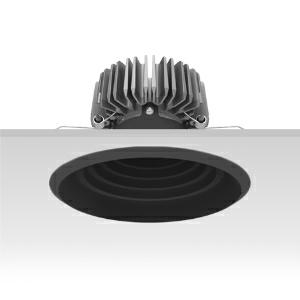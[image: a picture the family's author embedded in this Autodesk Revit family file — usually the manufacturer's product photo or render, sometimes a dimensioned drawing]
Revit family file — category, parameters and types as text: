
# Revit family: 3f_filippi_-_3f_reno_nero_ellittico_3f_filippi_-_31735_-_3f_reno_200_bk_4000-840_dali_ell
name_source: partatom
category: Lighting Fixtures
units: mm (PartAtom-declared; Revit-internal decimal feet)

## family parameters
Cut with Voids When Loaded = No
Host = Face
Light Source = No
Part Type = Normal
Room Calculation Point = No
Round Connector Dimension = Use Diameter
Shared = No

## types (1)
- 3F Filippi - 3F Reno Nero Ellittico (1 x LED, 3353 lm, 36 W, 4000 K)
    Apparent Load = 36 VA
    Approval mark = CE
    CIE Flux Codes = 81 100 100 100 100
    Color Rendering = 80
    Color Temperature = 4000 K
    Control Gear = Electronic transformer
    Default Elevation = 1800 mm
    Description = ILLUMINOTECHNICAL
Luminous efficiency 100% (DLOR 100%, ULOR 0%).
Initial luminous flux of the luminaire 3353 lm.
Direct symmetric elliptical distribution.
Installation Interdistance Transv.D = 0.77 x hu - Long.D = 1.51 x hu.
Tabular UGR (CIE 117 - 4H-8H; S=0.25H; 70/50/20): RUG 18 - 23.5.
Beam angle: 62° - 92°.
Luminous efficacy 93 lm/W.
Lifetime (L90/B10): 30000 h. (tq+25°C)
Lifetime (L85/B10): 50000 h. (tq+25°C)
Lifetime (L70/B10): 80000 h. (tq+25°C)
Sudden decreased luminous flux after 50000 hours: 0% (C0).
Photobiological safety in compliance with IEC/TR 62778: RG1 low risk, (IEC 62471).
In compliance with IEC/EN 62722-2-1 - IEC/EN 62717 standards.

SOURCE
Compact LED module 4000/840.
Energy efficiency class (UE 2019/2020 - UE 2019/2015): D.
CIE 13.3 Colour rendering index: CRI >80 (R9 <50%).
IES TM-30 Fidelity Index: Rf = 84 Rg = 95.
CCT nominal colour temperature 4000 K.
Colour initial tolerance (MacAdam): SDCM 3.
Zhaga Book 3 compliant.

MECHANICAL
Passive heat dissipator in die-casting aluminium, oversized, for optimum thermal management of the LED module.
Parabolic element with graduated/concentric rings in black polycarbonate.
Internal specular metallic louvre to optimise control of the luminous flux in polycarbonate.
Transparent external lens with glossy and satin differentiated surfaces, with a cooling and anti-insect system in methacrylate (PMMA).
Fastening spring clips in stainless steel.
Dimensions: diameter 216 mm, height 142 mm. Weight 1.505 kg.
IP44 protection degree for exposed part, IP20 for recessed part.
Mechanical strength to impacts IK04 (0.5 joule).
Glow-wire test resistance 650°C.

ELECTRICAL
Wiring on a separate unit.
Halogen Free DALI-2 DATI (Parts 251, 252, 253), PUSH-DIM, electronic wiring 230V-50/60Hz, power factor 0.97 at full load, THD <25%, constant output current, SELV, class II, 1 driver, 1 DALI addresse.
Power of the luminaire 36 W.
ENEC - CE.
SAFE FLICKER: PstLM=<1 and SVM=<0.4 (IEC TR 61547-1 and IEC TR 63158), to ensure a more comfortable and safe light.
Luminaire compliant with EN 60598-2-22 for power supply from a centralised emergency system CPSS (Central Power Supply System), not incorporated in the luminaire - high risk areas excluded. The default power and flux are 100% in AC and 100% in DC.
Ambient temperature from 0°C to +25°C.
Temperature class T6 max 85°C.
Relative humidity UR: <85%.

INSTALLATION
Pull-up recessed fitting.
False ceiling carving: 200 mm.
All accessories dedicated to this product are available on the Catalog and on our website www.3F-Filippi.com.

APPLICATIONS
Environments: architectural, commercial, exhibition areas, transit areas, corridors, shops, display windows, service areas.
In false ceilings with narrow voids.

LIGHT MANAGEMENT
Recommended minimum setting: 10%.
The luminaire, equipped with (DALI-2 DATI) driver, can be controlled manually with 3F Easy Dim technology or automatically/manually with wired or wireless DALI/D2D control systems.
The D2D driver guarantees interoperability with other devices with the same certification by making the following information available:
Device Data (Part 251), Energy Report (Part 252), Diagnosis & Maintenance (Part 253).
In electrical systems without a regulation system (manual or automatic) and DALI bus, a suitable jumper must be made on the DA-DA terminals of the appliance.

WARNING
Luminaire designed for disposal/recycling at end-of-life.
Replaceable (LED only) light source by a professional. Replaceable control gear by a professional.
    Height = 0 mm  [stored 0 ft]
    Lamp = 1 x LED
    Lamp Light Flux = 3353 lm
    Lamp Power = 36 W
    Lamp count = 1
    Length = 216 mm
    Lifetime = 50000 h
    Luminous efficacy = 93 lm/W
    Manufacturer = 3F Filippi
    ModVariant = No
    Model = 3F Filippi - 31735 - 3F Reno 200 BK 4000-840 DALI ELL
    Mounting Place = Ceiling
    Mounting Type = Recessed
    Number of Poles = 1
    OnlyDefault = Yes
    Power Factor = 1
    Product Name = 3F Filippi - 3F Reno Nero Ellittico
    Product group = recessed luminaire
    ProductGroupID = 4
    Protection Class = Protection class II
    Protection Degree = IP 20
    RLX_Detail_Level = 1
    RLX_Emergency_Light_Flux = 0 lm
    RLX_Emergency_Type = 0
    RLX_Emergency_Type_DB = No
    RlxData = <blob elided: 95293 chars, md5=32dcfa64>
    Socket = socket
    Standby Power = 0 W
    System Light Flux = 3353 lm
    System Power = 36 W
    Type Comments = Product without accessories
    Type Image = 3ffilippi_3f_reno_200_bk_2500_3000_4000.jpg
    URL = http://relux.com
    VarID = ---
    Voltage = 0 V
    Weight = 0.00 kg
    Width = 0 mm  [stored 0 ft]

note: [stored X ft] marks values corroborated as IEEE doubles in the binary element streams (Revit-internal decimal feet)

## geometry (parser evidence)
native form markers: Blend x4, Sweep x10
no freeform markers — native parametric forms only
